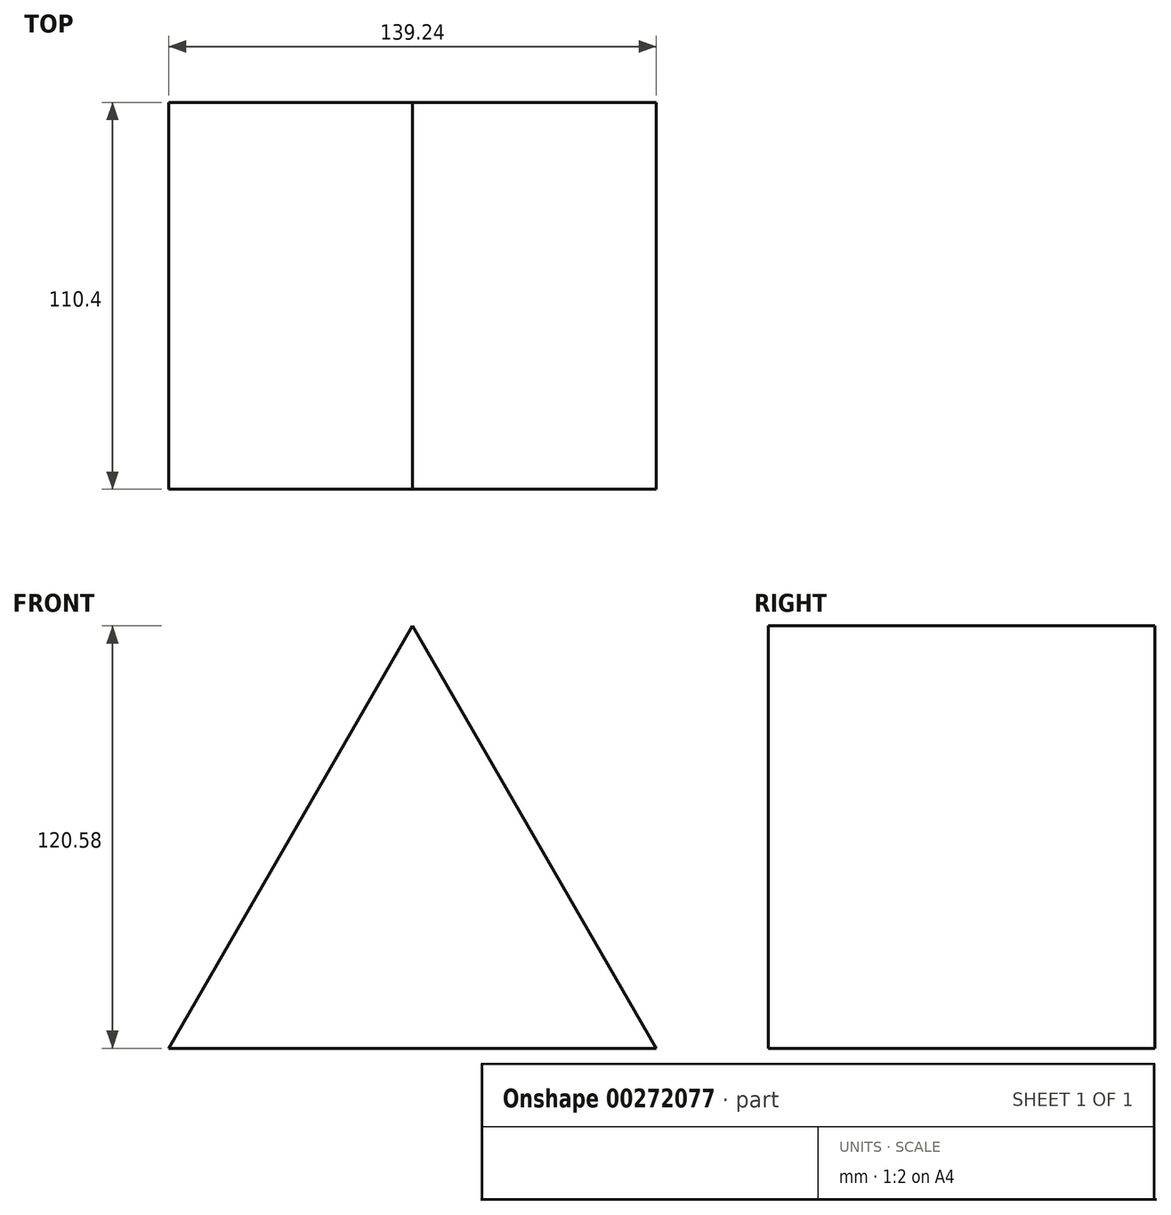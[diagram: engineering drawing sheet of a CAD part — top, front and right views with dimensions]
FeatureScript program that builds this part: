
annotation { "Feature Type Name" : "Feature", "Feature Type Description" : "" }
export const myFeature = defineFeature(function(context is Context, id is Id, definition is map)
    precondition{}
    {
        {
            var Q0;
            Q0=qCreatedBy(makeId("Front.planeOp"),FACE);
            var sketch = newSketch(context, id + "F0", { "sketchPlane" : qUnion([Q0])});
            skCircle(sketch, "E0.cCircle", {"center": v(0, 40.2) * mm, "radius": 40.2 * mm, "construction": true});
            skLineSegment(sketch, "E0.0", {"start": v(69.62, 0) * mm, "end": v(-69.62, 0) * mm});
            skLineSegment(sketch, "E0.1", {"start": v(-69.62, 0) * mm, "end": v(0, 120.58) * mm});
            skLineSegment(sketch, "E0.2", {"start": v(0, 120.58) * mm, "end": v(69.62, 0) * mm});
            skPoint(sketch, "E0.0.midPoint", {"position": v(0, 0) * mm});
            skSolve(sketch);
        }
        {
            var Q0;
            Q0=makeQuery(id+"F0.imprint","IMPRINT",FACE,{"disambiguationData":[TD([[makeQuery(id+"F0.imprint","IMPRINT",EDGE,{"derivedFrom":sQuery(id+"F0.wireOp",EDGE,"E0.0")}),-1.0]])]});
            extrude(context, id + "F1", {"entities" : qUnion([Q0]), "depth" : 110.4 * mm});
        }
    });
